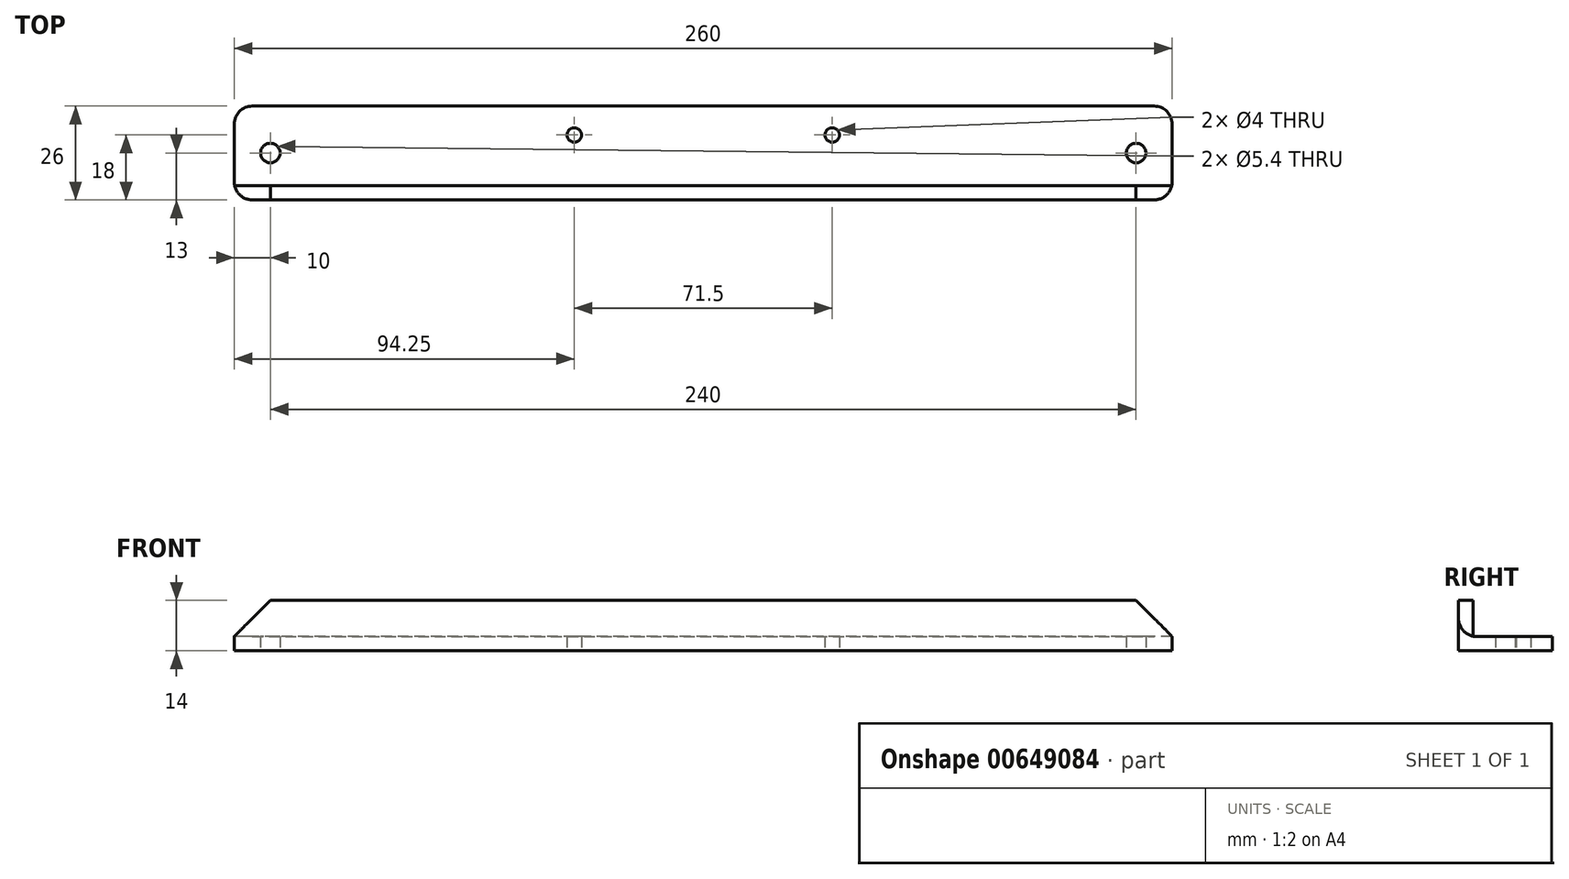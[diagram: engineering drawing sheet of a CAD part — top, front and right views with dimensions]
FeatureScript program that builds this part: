
annotation { "Feature Type Name" : "Feature", "Feature Type Description" : "" }
export const myFeature = defineFeature(function(context is Context, id is Id, definition is map)
    precondition{}
    {
        {
            var Q0;
            Q0=qCreatedBy(makeId("Top.planeOp"),FACE);
            var sketch = newSketch(context, id + "F0", { "sketchPlane" : qUnion([Q0])});
            skLineSegment(sketch, "E0.bottom", {"start": v(-130, -13) * mm, "end": v(130, -13) * mm});
            skLineSegment(sketch, "E0.top", {"start": v(-130, 13) * mm, "end": v(130, 13) * mm});
            skLineSegment(sketch, "E0.left", {"start": v(-130, -13) * mm, "end": v(-130, 13) * mm});
            skLineSegment(sketch, "E0.right", {"start": v(130, -13) * mm, "end": v(130, 13) * mm});
            skPoint(sketch, "E0.middle", {"position": v(0, 0) * mm});
            skCircle(sketch, "E1", {"center": v(120, 0) * mm, "radius": 2.7 * mm});
            skCircle(sketch, "E2", {"center": v(-120, 0) * mm, "radius": 2.7 * mm});
            skCircle(sketch, "E3", {"center": v(-35.75, 5) * mm, "radius": 2 * mm});
            skCircle(sketch, "E4", {"center": v(35.75, 5) * mm, "radius": 2 * mm});
            skLineSegment(sketch, "E5", {"start": v(-35.75, 5) * mm, "end": v(35.75, 5) * mm, "construction": true});
            skPoint(sketch, "E6", {"position": v(0, 5) * mm});
            skSolve(sketch);
        }
        {
            var Q0;
            Q0 = qSketchRegion(id + "F0", true);
            extrude(context, id + "F1", {"entities" : qUnion([Q0]), "depth" : 4 * mm, "offsetDistance" : 25 * mm});
        }
        {
            var Q0;
            Q0=makeQuery(id+"F1.opExtrude","CAP_FACE",FACE,{"disambiguationData":[OSD([sQuery(id+"F0.wireOp",EDGE,"E0.bottom"),sQuery(id+"F0.wireOp",EDGE,"E0.top"),sQuery(id+"F0.wireOp",EDGE,"E0.left"),sQuery(id+"F0.wireOp",EDGE,"E0.right"),sQuery(id+"F0.wireOp",EDGE,"E1"),sQuery(id+"F0.wireOp",EDGE,"E2"),sQuery(id+"F0.wireOp",EDGE,"E3"),sQuery(id+"F0.wireOp",EDGE,"E4")])],"isStart":false});
            var sketch = newSketch(context, id + "F2", { "sketchPlane" : qUnion([Q0])});
            skLineSegment(sketch, "E7.bottom", {"start": v(130, -13) * mm, "end": v(-130, -13) * mm});
            skLineSegment(sketch, "E7.top", {"start": v(130, -9) * mm, "end": v(-130, -9) * mm});
            skLineSegment(sketch, "E7.left", {"start": v(130, -13) * mm, "end": v(130, -9) * mm});
            skLineSegment(sketch, "E7.right", {"start": v(-130, -13) * mm, "end": v(-130, -9) * mm});
            skSolve(sketch);
        }
        {
            var Q0;
            Q0=makeQuery(id+"F2.imprint","IMPRINT",FACE,{"disambiguationData":[TD([[makeQuery(id+"F2.imprint","IMPRINT",EDGE,{"derivedFrom":sQuery(id+"F2.wireOp",EDGE,"E7.bottom")}),1.0]])]});
            extrude(context, id + "F3", {"entities" : qUnion([Q0]), "operationType" : NewBodyOperationType.ADD, "depth" : 10 * mm, "offsetDistance" : 25 * mm});
        }
        {
            var Q0;
            Q0=makeQuery(id+"F3.opExtrude","CAP_EDGE",EDGE,{"disambiguationData":[OSD([sQuery(id+"F2.wireOp",EDGE,"E7.right")])],"isStart":false});
            var Q1;
            Q1=makeQuery(id+"F3.opExtrude","CAP_EDGE",EDGE,{"disambiguationData":[OSD([sQuery(id+"F2.wireOp",EDGE,"E7.left")])],"isStart":false});
            chamfer(context, id + "F4", {"entities" : qUnion([Q0, Q1]), "width" : 10 * mm, "tangentPropagation" : true});
        }
        {
            var Q0;
            Q0=makeQuery(id+"F1.opExtrude","SWEPT_EDGE",EDGE,{"disambiguationData":[OSD([sQuery(id+"F0.wireOp",EDGE,"E0.top"),sQuery(id+"F0.wireOp",EDGE,"E0.right")])]});
            var Q1;
            Q1=makeQuery(id+"F3.boolean.opBoolean","MERGE",EDGE,{"derivedFrom":[makeQuery(id+"F1.opExtrude","SWEPT_EDGE",EDGE,{"disambiguationData":[OSD([sQuery(id+"F0.wireOp",EDGE,"E0.bottom"),sQuery(id+"F0.wireOp",EDGE,"E0.right")])]}),makeQuery(id+"F3.opExtrude","SWEPT_EDGE",EDGE,{"disambiguationData":[OSD([sQuery(id+"F2.wireOp",EDGE,"E7.bottom"),sQuery(id+"F2.wireOp",EDGE,"E7.left")])]})]});
            var Q2;
            Q2=makeQuery(id+"F1.opExtrude","SWEPT_EDGE",EDGE,{"disambiguationData":[OSD([sQuery(id+"F0.wireOp",EDGE,"E0.top"),sQuery(id+"F0.wireOp",EDGE,"E0.left")])]});
            var Q3;
            Q3=makeQuery(id+"F3.boolean.opBoolean","MERGE",EDGE,{"derivedFrom":[makeQuery(id+"F1.opExtrude","SWEPT_EDGE",EDGE,{"disambiguationData":[OSD([sQuery(id+"F0.wireOp",EDGE,"E0.bottom"),sQuery(id+"F0.wireOp",EDGE,"E0.left")])]}),makeQuery(id+"F3.opExtrude","SWEPT_EDGE",EDGE,{"disambiguationData":[OSD([sQuery(id+"F2.wireOp",EDGE,"E7.bottom"),sQuery(id+"F2.wireOp",EDGE,"E7.right")])]})]});
            fillet(context, id + "F5", {"entities" : qUnion([Q0, Q1, Q2, Q3]), "radius" : 5 * mm, "tangentPropagation" : true, "allowEdgeOverflow" : false});
        }
    });
